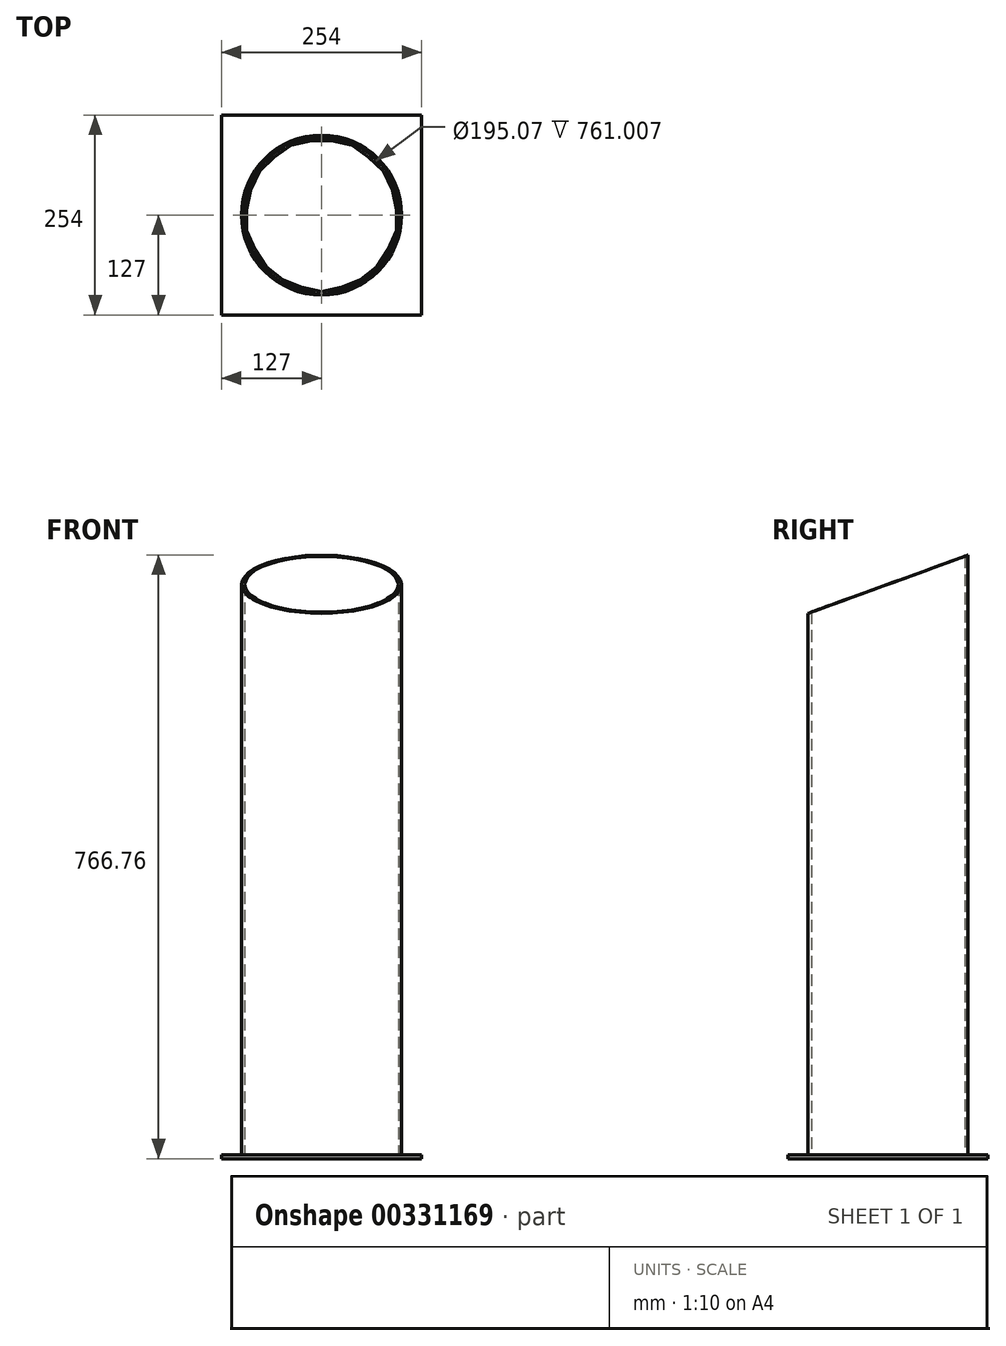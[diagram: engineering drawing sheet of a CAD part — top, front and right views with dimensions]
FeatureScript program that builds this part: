
annotation { "Feature Type Name" : "Feature", "Feature Type Description" : "" }
export const myFeature = defineFeature(function(context is Context, id is Id, definition is map)
    precondition{}
    {
        {
            var Q0;
            Q0=qCreatedBy(makeId("Top.planeOp"),FACE);
            var sketch = newSketch(context, id + "F0", { "sketchPlane" : qUnion([Q0])});
            skCircle(sketch, "E0", {"center": v(0, 0) * mm, "radius": 101.6 * mm});
            skCircle(sketch, "E1.0", {"center": v(0, 0) * mm, "radius": 97.54 * mm});
            skSolve(sketch);
        }
        {
            var Q0;
            Q0 = qSketchRegion(id + "F0", true);
            extrude(context, id + "F1", {"entities" : qUnion([Q0]), "depth" : 762 * mm});
        }
        {
            var Q0;
            Q0=qCreatedBy(makeId("Top.planeOp"),FACE);
            var sketch = newSketch(context, id + "F2", { "sketchPlane" : qUnion([Q0])});
            skLineSegment(sketch, "E2.bottom", {"start": v(127, 127) * mm, "end": v(-127, 127) * mm});
            skLineSegment(sketch, "E2.top", {"start": v(127, -127) * mm, "end": v(-127, -127) * mm});
            skLineSegment(sketch, "E2.left", {"start": v(127, 127) * mm, "end": v(127, -127) * mm});
            skLineSegment(sketch, "E2.right", {"start": v(-127, 127) * mm, "end": v(-127, -127) * mm});
            skPoint(sketch, "E2.middle", {"position": v(0, 0) * mm});
            skSolve(sketch);
        }
        {
            var Q0;
            Q0 = qSketchRegion(id + "F2", true);
            extrude(context, id + "F3", {"entities" : qUnion([Q0]), "operationType" : NewBodyOperationType.ADD, "oppositeDirection" : true, "depth" : 4.76 * mm});
        }
        {
            var Q0;
            Q0=qCreatedBy(makeId("Right.planeOp"),FACE);
            var sketch = newSketch(context, id + "F4", { "sketchPlane" : qUnion([Q0])});
            skPoint(sketch, "E3.middle", {"position": v(0, 441.03) * mm});
            skPoint(sketch, "E3.top.start.orphan", {"position": v(-208.83, 272.47) * mm});
            skPoint(sketch, "E3.right.start.orphan", {"position": v(208.83, 609.6) * mm});
            skPoint(sketch, "E4.orphan", {"position": v(412.03, 609.6) * mm});
            skPoint(sketch, "E5.start.orphan", {"position": v(-412.03, 272.47) * mm});
            skLineSegment(sketch, "E6.bottom", {"start": v(101.6, 762) * mm, "end": v(-101.6, 762) * mm});
            skLineSegment(sketch, "E6.right", {"start": v(-101.6, 762) * mm, "end": v(-101.6, 688.04) * mm});
            skPoint(sketch, "E6.middle", {"position": v(0, 725.02) * mm});
            skLineSegment(sketch, "E7", {"start": v(-101.6, 688.04) * mm, "end": v(101.6, 762) * mm});
            skPoint(sketch, "E6.top.start.orphan", {"position": v(101.6, 688.04) * mm});
            skSolve(sketch);
        }
        {
            var Q0;
            Q0 = qSketchRegion(id + "F4", true);
            extrude(context, id + "F5", {"entities" : qUnion([Q0]), "operationType" : NewBodyOperationType.REMOVE, "endBound" : BoundingType.THROUGH_ALL, "oppositeDirection" : true, "depth" : 25.4 * mm, "hasSecondDirection" : true, "secondDirectionBound" : SecondDirectionBoundingType.THROUGH_ALL, "secondDirectionOppositeDirection" : false, "secondDirectionDepth" : 25.4 * mm});
        }
        {
            var Q0;
            Q0 = qSketchRegion(id + "F4", true);
            extrude(context, id + "F6", {"entities" : qUnion([Q0]), "operationType" : NewBodyOperationType.REMOVE, "endBound" : BoundingType.THROUGH_ALL, "depth" : 25.4 * mm, "hasSecondDirection" : true, "secondDirectionBound" : SecondDirectionBoundingType.THROUGH_ALL, "secondDirectionOppositeDirection" : true, "secondDirectionDepth" : 25.4 * mm});
        }
    });
